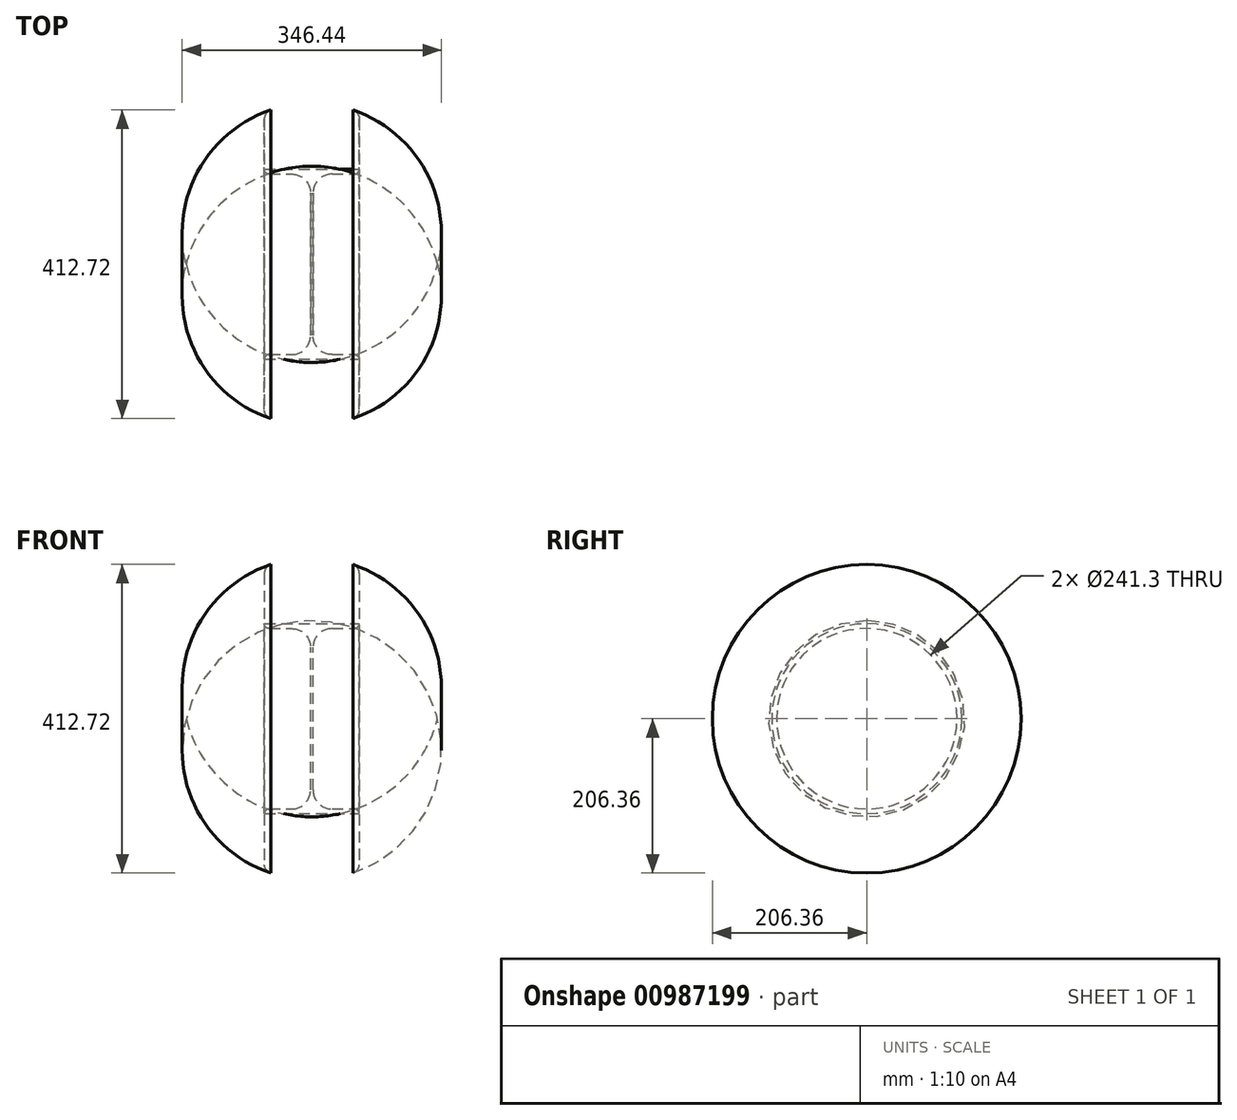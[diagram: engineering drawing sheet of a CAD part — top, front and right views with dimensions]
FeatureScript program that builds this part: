
annotation { "Feature Type Name" : "Feature", "Feature Type Description" : "" }
export const myFeature = defineFeature(function(context is Context, id is Id, definition is map)
    precondition{}
    {
        {
            var Q0;
            Q0=qCreatedBy(makeId("Top.planeOp"),FACE);
            var sketch = newSketch(context, id + "F0", { "sketchPlane" : qUnion([Q0])});
            skLineSegment(sketch, "E0", {"start": v(0, 0) * mm, "end": v(-48.75, 0) * mm});
            skSolve(sketch);
        }
        {
            var Q0;
            Q0=qCreatedBy(makeId("Front.planeOp"),FACE);
            var sketch = newSketch(context, id + "F1", { "sketchPlane" : qUnion([Q0])});
            skLineSegment(sketch, "E1.left", {"start": v(-63.5, 203.2) * mm, "end": v(-63.5, 127) * mm});
            skLineSegment(sketch, "E1.right", {"start": v(63.5, 203.2) * mm, "end": v(63.5, 127) * mm});
            skArc(sketch, "E2", {"start": v(63.5, 203.2) * mm, "mid": v(0, 215.26) * mm, "end": v(-63.5, 203.2) * mm});
            skLineSegment(sketch, "E3", {"start": v(-63.5, 127) * mm, "end": v(63.5, 127) * mm});
            skSolve(sketch);
        }
        {
            var Q0;
            Q0=makeQuery(id+"F1.imprint","IMPRINT",FACE,{"disambiguationData":[TD([[makeQuery(id+"F1.imprint","IMPRINT",EDGE,{"derivedFrom":sQuery(id+"F1.wireOp",EDGE,"E1.left")}),1.0]])]});
            var Q1;
            Q1=sQuery(id+"F0.wireOp",EDGE,"E0");
            revolve(context, id + "F2", {"surfaceOperationType" : NewSurfaceOperationType.NEW, "entities" : qUnion([Q0]), "axis" : qUnion([Q1]), "revolveType" : RevolveType.FULL});
        }
        {
            var Q0;
            Q0=makeQuery(id+"F2.opRevolve","SWEPT_EDGE",EDGE,{"disambiguationData":[OSD([sQuery(id+"F1.wireOp",EDGE,"E1.right"),sQuery(id+"F1.wireOp",EDGE,"E2")])]});
            var Q1;
            Q1=makeQuery(id+"F2.opRevolve","SWEPT_EDGE",EDGE,{"disambiguationData":[OSD([sQuery(id+"F1.wireOp",EDGE,"E1.left"),sQuery(id+"F1.wireOp",EDGE,"E2")])]});
            fillet(context, id + "F3", {"entities" : qUnion([Q0, Q1]), "radius" : 12.7 * mm, "tangentPropagation" : true, "allowEdgeOverflow" : false});
        }
        {
            var Q0;
            Q0=qCreatedBy(makeId("Front.planeOp"),FACE);
            var sketch = newSketch(context, id + "F4", { "sketchPlane" : qUnion([Q0])});
            skLineSegment(sketch, "E4.top", {"start": v(-57.15, 120.65) * mm, "end": v(-26.99, 120.65) * mm});
            skLineSegment(sketch, "E5.top", {"start": v(-1.59, 0) * mm, "end": v(1.59, 0) * mm});
            skLineSegment(sketch, "E5.left", {"start": v(-1.59, 95.25) * mm, "end": v(-1.59, 0) * mm});
            skLineSegment(sketch, "E5.right", {"start": v(1.59, 95.25) * mm, "end": v(1.59, 0) * mm});
            skLineSegment(sketch, "E6.trimOffspring", {"start": v(26.99, 120.65) * mm, "end": v(57.15, 120.65) * mm});
            skPoint(sketch, "E7.visualSharp", {"position": v(-1.59, 120.65) * mm});
            skPoint(sketch, "E8.visualSharp", {"position": v(1.59, 120.65) * mm});
            skArc(sketch, "E8.filletArc", {"start": v(26.99, 120.65) * mm, "mid": v(9.03, 113.21) * mm, "end": v(1.59, 95.25) * mm});
            skArc(sketch, "E9.filletArc", {"start": v(-1.59, 95.25) * mm, "mid": v(-9.03, 113.21) * mm, "end": v(-26.99, 120.65) * mm});
            skPoint(sketch, "E10.visualSharp", {"position": v(-63.5, 120.65) * mm});
            skArc(sketch, "E10.filletArc", {"start": v(-63.5, 127) * mm, "mid": v(-61.64, 122.5) * mm, "end": v(-57.15, 120.65) * mm});
            skPoint(sketch, "E11.visualSharp", {"position": v(63.5, 120.65) * mm});
            skArc(sketch, "E11.filletArc", {"start": v(57.15, 120.65) * mm, "mid": v(61.64, 122.5) * mm, "end": v(63.5, 127) * mm});
            skLineSegment(sketch, "E12", {"start": v(-63.5, 127) * mm, "end": v(63.5, 127) * mm});
            skSolve(sketch);
        }
        {
            var Q0;
            Q0=makeQuery(id+"F4.imprint","IMPRINT",FACE,{"disambiguationData":[TD([[makeQuery(id+"F4.imprint","IMPRINT",EDGE,{"derivedFrom":sQuery(id+"F4.wireOp",EDGE,"E4.top")}),1.0]])]});
            var Q1;
            Q1=sQuery(id+"F0.wireOp",EDGE,"E0");
            revolve(context, id + "F5", {"surfaceOperationType" : NewSurfaceOperationType.NEW, "entities" : qUnion([Q0]), "axis" : qUnion([Q1]), "revolveType" : RevolveType.FULL});
        }
    });
